# Revit family: Serene_T&T_Door_Custom
name_source: partatom
category: Doors
revit_build: Autodesk Revit 2014 (Build: 20130308_1515(x64)
units: mm (PartAtom-declared; Revit-internal decimal feet)

## types (1)
- Serene_T&T_Door_Custom
    Custom Door Exterior Offset = 0 mm  [stored 0 ft]
    Custom Door Height = 2090 mm  [stored 6.85696 ft]
    Custom Door Width = 690 mm  [stored 2.26378 ft]
    Custom Windload = 1000 mm  [stored 3.28084 ft]
    DG Gasket Finish = Double Glazing Gasket Material
    DG Thickness Calc = 4 mm  [stored 0.0131234 ft]
    Default Sill Height = 0 mm  [stored 0 ft]
    Description = Heavy duty tilt and hinged door, custom
    Frame Thickness = 52 mm
    Height = 2090 mm  [stored 6.85696 ft]
    Limit Door Height Max = 2767 mm
    Limit Door Height Min = 367 mm
    Limit Door Width Max = 1267 mm
    Limit Door Width Min = 367 mm
    Limit Sash Height Max = 2700 mm  [stored 8.85827 ft]
    Limit Sash Height Min = 300 mm
    Limit Sash Width Max = 1200 mm
    Limit Sash Width Min = 300 mm
    Manufacturer = Crealco
    Max Pane Area = 0.88 m²
    Max System DG One Piece Thickness = 6 mm  [stored 0.019685 ft]
    Max System DG Unit Thickness = 25 mm  [stored 0.082021 ft]
    Model = Serene
    Sash Edge Gap = 34 mm
    Sash Frame Gasket = 3 mm  [stored 0.00984252 ft]
    Sash Height = 2023 mm
    Sash Width = 623 mm
    URL = http://www.crealco.co.za
    Wall Closure = By host
    Width = 690 mm  [stored 2.26378 ft]
    Windload Design = 1000 mm  [stored 3.28084 ft]

note: [stored X ft] marks values corroborated as IEEE doubles in the binary element streams (Revit-internal decimal feet)

## geometry (parser evidence)
native form markers: Sweep x11
no freeform markers — native parametric forms only
